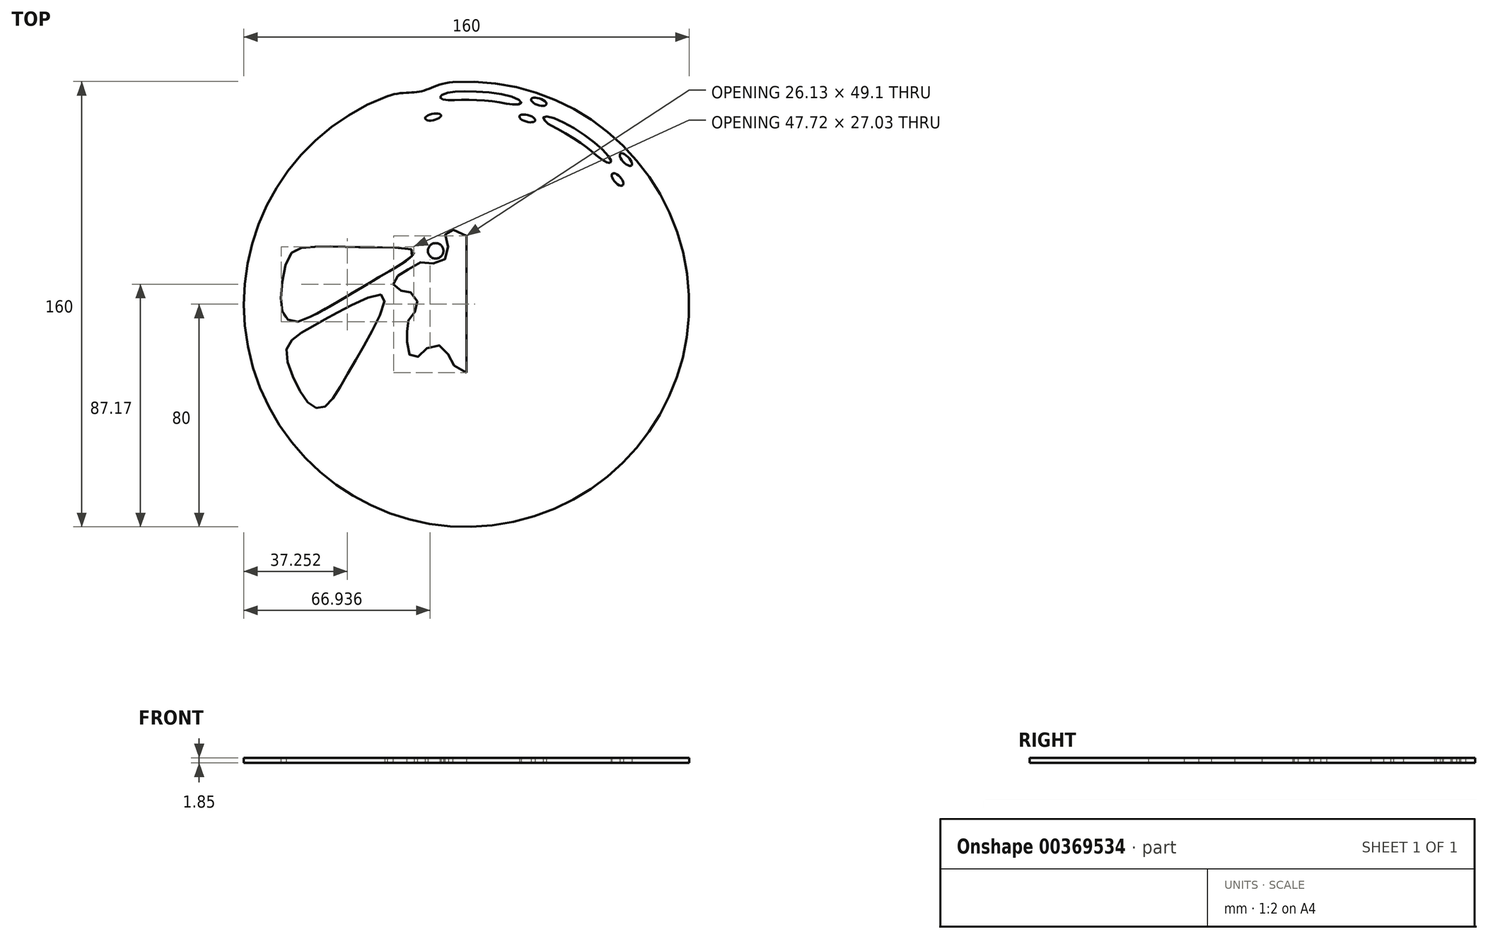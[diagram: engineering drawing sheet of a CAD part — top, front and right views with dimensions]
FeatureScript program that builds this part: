
annotation { "Feature Type Name" : "Feature", "Feature Type Description" : "" }
export const myFeature = defineFeature(function(context is Context, id is Id, definition is map)
    precondition{}
    {
        {
            var Q0;
            Q0=qCreatedBy(makeId("Front.planeOp"),FACE);
            var sketch = newSketch(context, id + "F0", { "sketchPlane" : qUnion([Q0])});
            skLineSegment(sketch, "E0", {"start": v(0, 138.64) * mm, "end": v(0, -83.7) * mm, "construction": true});
            skSolve(sketch);
        }
        {
            var Q0;
            Q0=qCreatedBy(makeId("Front.planeOp"),FACE);
            var sketch = newSketch(context, id + "F1", { "sketchPlane" : qUnion([Q0])});
            skLineSegment(sketch, "E1", {"start": v(0, 99.06) * mm, "end": v(0, -156.55) * mm, "construction": true});
            skSolve(sketch);
        }
        {
            var Q0;
            Q0=qCreatedBy(makeId("Front.planeOp"),FACE);
            var sketch = newSketch(context, id + "F2", { "sketchPlane" : qUnion([Q0])});
            skLineSegment(sketch, "E2", {"start": v(0, 90.89) * mm, "end": v(0, -102.4) * mm, "construction": true});
            skSolve(sketch);
        }
        {
            var Q0;
            Q0=qCreatedBy(makeId("Front.planeOp"),FACE);
            var sketch = newSketch(context, id + "F3", { "sketchPlane" : qUnion([Q0])});
            skLineSegment(sketch, "E3", {"start": v(0, 71.11) * mm, "end": v(0, -97.76) * mm, "construction": true});
            skSolve(sketch);
        }
        {
            var Q0;
            Q0=qCreatedBy(makeId("Right.planeOp"),FACE);
            var sketch = newSketch(context, id + "F4", { "sketchPlane" : qUnion([Q0])});
            skLineSegment(sketch, "E4", {"start": v(0, 122.7) * mm, "end": v(0, -125.95) * mm, "construction": true});
            skSolve(sketch);
        }
        {
            var Q0;
            Q0=qCreatedBy(makeId("Top.planeOp"),FACE);
            var sketch = newSketch(context, id + "F5", { "sketchPlane" : qUnion([Q0])});
            skCircle(sketch, "E5", {"center": v(0, 0) * mm, "radius": 80 * mm});
            skSolve(sketch);
        }
        {
            var Q0;
            Q0 = qSketchRegion(id + "F5", true);
            extrude(context, id + "F6", {"entities" : qUnion([Q0]), "depth" : 1.85 * mm});
        }
        {
            var Q0;
            Q0=qCreatedBy(makeId("Top.planeOp"),FACE);
            var sketch = newSketch(context, id + "F7", { "sketchPlane" : qUnion([Q0])});
            skFitSpline(sketch, "E6", {"points": [v(-64.63, -16.23) * mm, v(-60.3, -10.94) * mm, v(-52.05, -6.16) * mm, v(-40.29, 0.16) * mm, v(-29.87, 3.08) * mm, v(-32.11, -6.06) * mm, v(-39.8, -19.97) * mm, v(-46.31, -31.32) * mm, v(-51.4, -37.06) * mm, v(-55.83, -36.34) * mm, v(-61.8, -27.17) * mm, v(-64.63, -16.23) * mm]});
            skSolve(sketch);
        }
        {
            var Q0;
            Q0 = qSketchRegion(id + "F7", true);
            extrude(context, id + "F8", {"entities" : qUnion([Q0]), "operationType" : NewBodyOperationType.REMOVE, "endBound" : BoundingType.THROUGH_ALL, "depth" : 25.4 * mm});
        }
        {
            var Q0;
            Q0=qCreatedBy(makeId("Top.planeOp"),FACE);
            var sketch = newSketch(context, id + "F9", { "sketchPlane" : qUnion([Q0])});
            skFitSpline(sketch, "E7", {"points": [v(-62.85, 18.43) * mm, v(-56.02, 20.54) * mm, v(-44.06, 20.64) * mm, v(-32.96, 20.43) * mm, v(-18.9, 18.95) * mm, v(-29.4, 10.91) * mm, v(-42.54, 3.08) * mm, v(-53.37, -3.16) * mm, v(-62.05, -6.33) * mm, v(-65.79, -3.46) * mm, v(-66.31, 6.7) * mm, v(-62.85, 18.43) * mm]});
            skSolve(sketch);
        }
        {
            var Q0;
            Q0 = qSketchRegion(id + "F9", true);
            extrude(context, id + "F10", {"entities" : qUnion([Q0]), "operationType" : NewBodyOperationType.REMOVE, "endBound" : BoundingType.THROUGH_ALL, "depth" : 25.4 * mm});
        }
        {
            var Q0;
            Q0=qCreatedBy(makeId("Top.planeOp"),FACE);
            var sketch = newSketch(context, id + "F11", { "sketchPlane" : qUnion([Q0])});
            skCircle(sketch, "E8", {"center": v(-11.06, 19.17) * mm, "radius": 2.78 * mm});
            skSolve(sketch);
        }
        {
            var Q0;
            Q0 = qSketchRegion(id + "F11", true);
            extrude(context, id + "F12", {"entities" : qUnion([Q0]), "operationType" : NewBodyOperationType.REMOVE, "endBound" : BoundingType.THROUGH_ALL, "depth" : 25.4 * mm});
        }
        {
            var Q0;
            Q0=qCreatedBy(makeId("Top.planeOp"),FACE);
            var sketch = newSketch(context, id + "F13", { "sketchPlane" : qUnion([Q0])});
            skLineSegment(sketch, "E9", {"start": v(0, -24.55) * mm, "end": v(0, 24.55) * mm});
            skFitSpline(sketch, "E10", {"points": [v(0, -24.55) * mm, v(-5.24, -21.2) * mm, v(-7.8, -15.87) * mm, v(-13.23, -15.07) * mm, v(-17.09, -18.7) * mm, v(-19.97, -18.78) * mm, v(-21.28, -13.87) * mm, v(-21.36, -10.06) * mm, v(-20.9, -5.81) * mm, v(-18.56, -2.89) * mm, v(-17.7, 1.11) * mm, v(-20.21, 4.25) * mm, v(-23.23, 4.81) * mm, v(-26.26, 6.85) * mm, v(-25.2, 9.67) * mm, v(-21.3, 12.26) * mm, v(-15.65, 15.14) * mm, v(-10.27, 14.68) * mm, v(-6.43, 18.75) * mm, v(-7.67, 24.32) * mm, v(-6.07, 26.78) * mm, v(0, 24.55) * mm], "startDerivative": vector(-114.1, 76.06) * mm, "endDerivative": vector(64.61, -35.72) * mm});
            skSolve(sketch);
        }
        {
            var Q0;
            Q0 = qSketchRegion(id + "F13", true);
            extrude(context, id + "F14", {"entities" : qUnion([Q0]), "operationType" : NewBodyOperationType.REMOVE, "endBound" : BoundingType.THROUGH_ALL, "depth" : 25.4 * mm});
        }
        {
            var Q0;
            Q0=qCreatedBy(makeId("Top.planeOp"),FACE);
            var sketch = newSketch(context, id + "F15", { "sketchPlane" : qUnion([Q0])});
            skFitSpline(sketch, "E11", {"points": [v(-9.52, 74.4) * mm, v(-8.22, 75.48) * mm, v(0, 76.52) * mm, v(17.26, 74.28) * mm, v(19.69, 72.38) * mm, v(17.6, 71.7) * mm, v(12.15, 72.5) * mm, v(4.84, 73.28) * mm, v(-2.55, 73.39) * mm, v(-7.54, 73.39) * mm, v(-9.52, 74.4) * mm]});
            skSolve(sketch);
        }
        {
            var Q0;
            Q0 = qSketchRegion(id + "F15", true);
            extrude(context, id + "F16", {"entities" : qUnion([Q0]), "operationType" : NewBodyOperationType.REMOVE, "endBound" : BoundingType.THROUGH_ALL, "depth" : 25.4 * mm});
        }
        {
            var Q0;
            Q0=qCreatedBy(makeId("Top.planeOp"),FACE);
            var sketch = newSketch(context, id + "F17", { "sketchPlane" : qUnion([Q0])});
            skFitSpline(sketch, "E12", {"points": [v(51.59, 50.7) * mm, v(49.69, 51.31) * mm, v(44.66, 55.13) * mm, v(39.63, 58.9) * mm, v(30.78, 63.98) * mm, v(28.99, 65.1) * mm, v(27.54, 66.96) * mm, v(30.15, 67.25) * mm, v(45.36, 58.48) * mm, v(51.92, 51.64) * mm, v(51.59, 50.7) * mm]});
            skSolve(sketch);
        }
        {
            var Q0;
            Q0 = qSketchRegion(id + "F17", true);
            extrude(context, id + "F18", {"entities" : qUnion([Q0]), "operationType" : NewBodyOperationType.REMOVE, "endBound" : BoundingType.THROUGH_ALL, "depth" : 25.4 * mm});
        }
        {
            var Q0;
            Q0=qCreatedBy(makeId("Right.planeOp"),FACE);
            var sketch = newSketch(context, id + "F19", { "sketchPlane" : qUnion([Q0])});
            skLineSegment(sketch, "E13", {"start": v(0, 65.5) * mm, "end": v(0, -57.45) * mm, "construction": true});
            skSolve(sketch);
        }
        {
            var Q0;
            Q0=qCreatedBy(makeId("Top.planeOp"),FACE);
            var sketch = newSketch(context, id + "F20", { "sketchPlane" : qUnion([Q0])});
            skEllipse(sketch, "E14", {"center": v(21.85, 66.77) * mm, "majorRadius": 2.92 * mm, "minorRadius": 1.22 * mm, "majorAxis": v(0.96, -0.26)});
            skEllipse(sketch, "E15", {"center": v(25.97, 72.74) * mm, "majorRadius": 2.9 * mm, "minorRadius": 1.2 * mm, "majorAxis": v(0.94, -0.33)});
            skSolve(sketch);
        }
        {
            var Q0;
            Q0 = qSketchRegion(id + "F20", true);
            extrude(context, id + "F21", {"entities" : qUnion([Q0]), "operationType" : NewBodyOperationType.REMOVE, "endBound" : BoundingType.THROUGH_ALL, "depth" : 25.4 * mm});
        }
        {
            var Q0;
            Q0=qCreatedBy(makeId("Right.planeOp"),FACE);
            var sketch = newSketch(context, id + "F22", { "sketchPlane" : qUnion([Q0])});
            skLineSegment(sketch, "E16", {"start": v(0, 93.39) * mm, "end": v(0, -94.72) * mm, "construction": true});
            skSolve(sketch);
        }
        {
            var Q0;
            Q0=qCreatedBy(makeId("Top.planeOp"),FACE);
            var sketch = newSketch(context, id + "F23", { "sketchPlane" : qUnion([Q0])});
            skFitSpline(sketch, "E17", {"points": [v(-28.52, 74.75) * mm, v(-16.53, 76.44) * mm, v(-4.92, 79.85) * mm], "startDerivative": vector(30, 10.32) * mm, "endDerivative": vector(31.51, 2.99) * mm});
            skLineSegment(sketch, "E18", {"start": v(-28.52, 74.75) * mm, "end": v(-16.53, 76.44) * mm, "construction": true});
            skLineSegment(sketch, "E19", {"start": v(-16.53, 76.44) * mm, "end": v(-4.92, 79.85) * mm, "construction": true});
            skArc(sketch, "E20", {"start": v(-4.92, 79.85) * mm, "mid": v(-17.13, 79.18) * mm, "end": v(-28.52, 74.75) * mm});
            skSolve(sketch);
        }
        {
            var Q0;
            Q0 = qSketchRegion(id + "F23", true);
            extrude(context, id + "F24", {"entities" : qUnion([Q0]), "operationType" : NewBodyOperationType.REMOVE, "endBound" : BoundingType.THROUGH_ALL, "depth" : 25.4 * mm});
        }
        {
            var Q0;
            Q0=qCreatedBy(makeId("Right.planeOp"),FACE);
            var sketch = newSketch(context, id + "F25", { "sketchPlane" : qUnion([Q0])});
            skLineSegment(sketch, "E21", {"start": v(0, 66.1) * mm, "end": v(0, -70.88) * mm, "construction": true});
            skSolve(sketch);
        }
        {
            var Q0;
            Q0=qCreatedBy(makeId("Top.planeOp"),FACE);
            var sketch = newSketch(context, id + "F26", { "sketchPlane" : qUnion([Q0])});
            skEllipse(sketch, "E22", {"center": v(-12, 67.27) * mm, "majorRadius": 2.9 * mm, "minorRadius": 1.16 * mm, "majorAxis": v(0.98, 0.2)});
            skEllipse(sketch, "E23", {"center": v(57.25, 51.95) * mm, "majorRadius": 2.91 * mm, "minorRadius": 1.2 * mm, "majorAxis": v(0.69, -0.72)});
            skEllipse(sketch, "E24", {"center": v(54.27, 44.81) * mm, "majorRadius": 2.8 * mm, "minorRadius": 1.26 * mm, "majorAxis": v(0.66, -0.75)});
            skSolve(sketch);
        }
        {
            var Q0;
            Q0 = qSketchRegion(id + "F26", true);
            extrude(context, id + "F27", {"entities" : qUnion([Q0]), "operationType" : NewBodyOperationType.REMOVE, "endBound" : BoundingType.THROUGH_ALL, "depth" : 25.4 * mm});
        }
        {
            var Q0;
            Q0=qCreatedBy(makeId("Right.planeOp"),FACE);
            var sketch = newSketch(context, id + "F28", { "sketchPlane" : qUnion([Q0])});
            skLineSegment(sketch, "E25", {"start": v(0, 62.37) * mm, "end": v(0, -64.4) * mm, "construction": true});
            skSolve(sketch);
        }
    });
